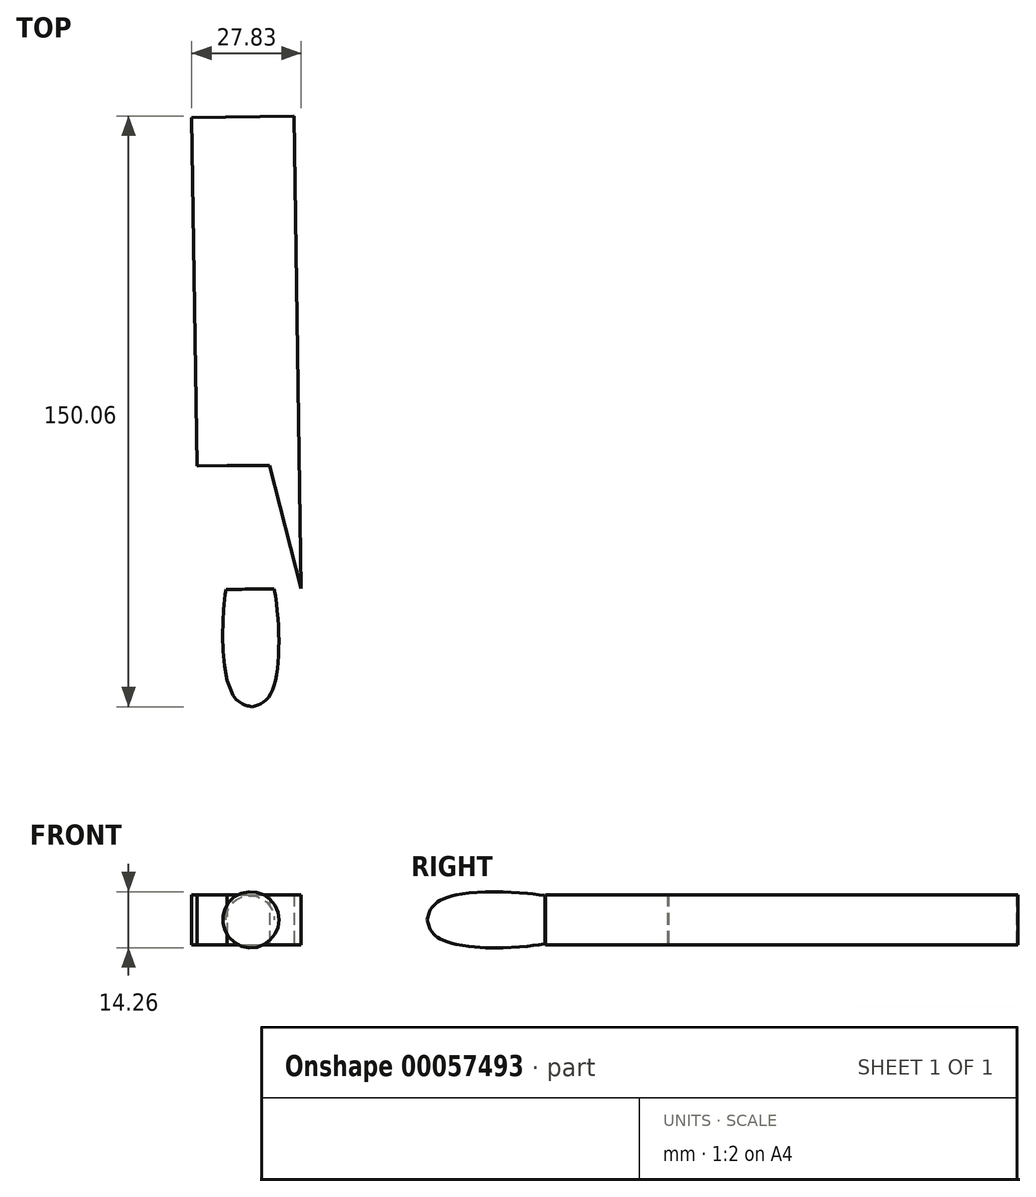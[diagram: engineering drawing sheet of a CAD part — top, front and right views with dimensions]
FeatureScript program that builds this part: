
annotation { "Feature Type Name" : "Feature", "Feature Type Description" : "" }
export const myFeature = defineFeature(function(context is Context, id is Id, definition is map)
    precondition{}
    {
        {
            var Q0;
            Q0=qCreatedBy(makeId("Top.planeOp"),FACE);
            var sketch = newSketch(context, id + "F0", { "sketchPlane" : qUnion([Q0])});
            skLineSegment(sketch, "E0", {"start": v(3.45, -15.9) * mm, "end": v(14.21, -15.9) * mm});
            skFitSpline(sketch, "E1", {"points": [v(14.21, -15.9) * mm, v(11.82, -26.67) * mm, v(15.89, -50.11) * mm, v(14.21, -74.5) * mm, v(8.95, -77.38) * mm], "startDerivative": vector(-17.1, -46.46) * mm, "endDerivative": vector(-37.4, -7.86) * mm});
            skLineSegment(sketch, "E2", {"start": v(8.83, -15.9) * mm, "end": v(9.79, -78.57) * mm, "construction": true});
            skLineSegment(sketch, "E3", {"start": v(8.83, -15.9) * mm, "end": v(7.48, 72.76) * mm, "construction": true});
            skLineSegment(sketch, "E4.0", {"start": v(22.3, -47.13) * mm, "end": v(20.48, 72.86) * mm});
            skLineSegment(sketch, "E5.0", {"start": v(-4.17, -16.1) * mm, "end": v(-5.52, 72.46) * mm});
            skLineSegment(sketch, "E6", {"start": v(-5.52, 72.46) * mm, "end": v(20.48, 72.86) * mm});
            skLineSegment(sketch, "E7", {"start": v(-4.17, -16.1) * mm, "end": v(22.3, -47.13) * mm});
            skLineSegment(sketch, "E8", {"start": v(8.83, -15.9) * mm, "end": v(9.77, -77.2) * mm});
            skLineSegment(sketch, "E9", {"start": v(22.3, -47.13) * mm, "end": v(-4.17, -16.1) * mm});
            skLineSegment(sketch, "E10", {"start": v(-4.17, -16.1) * mm, "end": v(3.45, -15.9) * mm});
            skLineSegment(sketch, "E11", {"start": v(14.21, -15.9) * mm, "end": v(22.3, -47.13) * mm});
            skLineSegment(sketch, "E12", {"start": v(8.83, -15.9) * mm, "end": v(-4.17, -16.1) * mm});
            skLineSegment(sketch, "E13.0", {"start": v(11.3, -157.3) * mm, "end": v(23.99, -157.11) * mm});
            skLineSegment(sketch, "E14", {"start": v(22.3, -47.13) * mm, "end": v(-6.38, -47.56) * mm});
            skSolve(sketch);
        }
        {
            var Q0;
            {var subQ3=sQuery(id+"F0.wireOp",EDGE,"E8");Q0=makeQuery(id+"F0.imprint","IMPRINT",FACE,{"disambiguationData":[TD([[makeQuery(id+"F0.imprint","IMPRINT",EDGE,{"derivedFrom":subQ3}),1.0]])]});}
            var Q1;
            Q1=sQuery(id+"F0.wireOp",EDGE,"E8");
            revolve(context, id + "F1", {"entities" : qUnion([Q0]), "axis" : qUnion([Q1]), "revolveType" : RevolveType.FULL});
        }
        {
            var Q0;
            Q0=makeQuery(id+"F0.imprint","IMPRINT",FACE,{"disambiguationData":[TD([[makeQuery(id+"F0.imprint","IMPRINT",EDGE,{"derivedFrom":sQuery(id+"F0.wireOp",EDGE,"E4.0")}),1.0]])]});
            extrude(context, id + "F2", {"entities" : qUnion([Q0]), "depth" : 6.35 * mm});
        }
        {
            var Q0;
            Q0=makeQuery(id+"F2.opExtrude","CAP_FACE",FACE,{"disambiguationData":[OSD([sQuery(id+"F0.wireOp",EDGE,"E0"),sQuery(id+"F0.wireOp",EDGE,"E4.0"),sQuery(id+"F0.wireOp",EDGE,"E5.0"),sQuery(id+"F0.wireOp",EDGE,"E9"),sQuery(id+"F0.wireOp",EDGE,"E6"),sQuery(id+"F0.wireOp",EDGE,"E10")])],"isStart":true});
            extrude(context, id + "F3", {"entities" : qUnion([Q0]), "operationType" : NewBodyOperationType.ADD, "depth" : 6.35 * mm});
        }
    });
